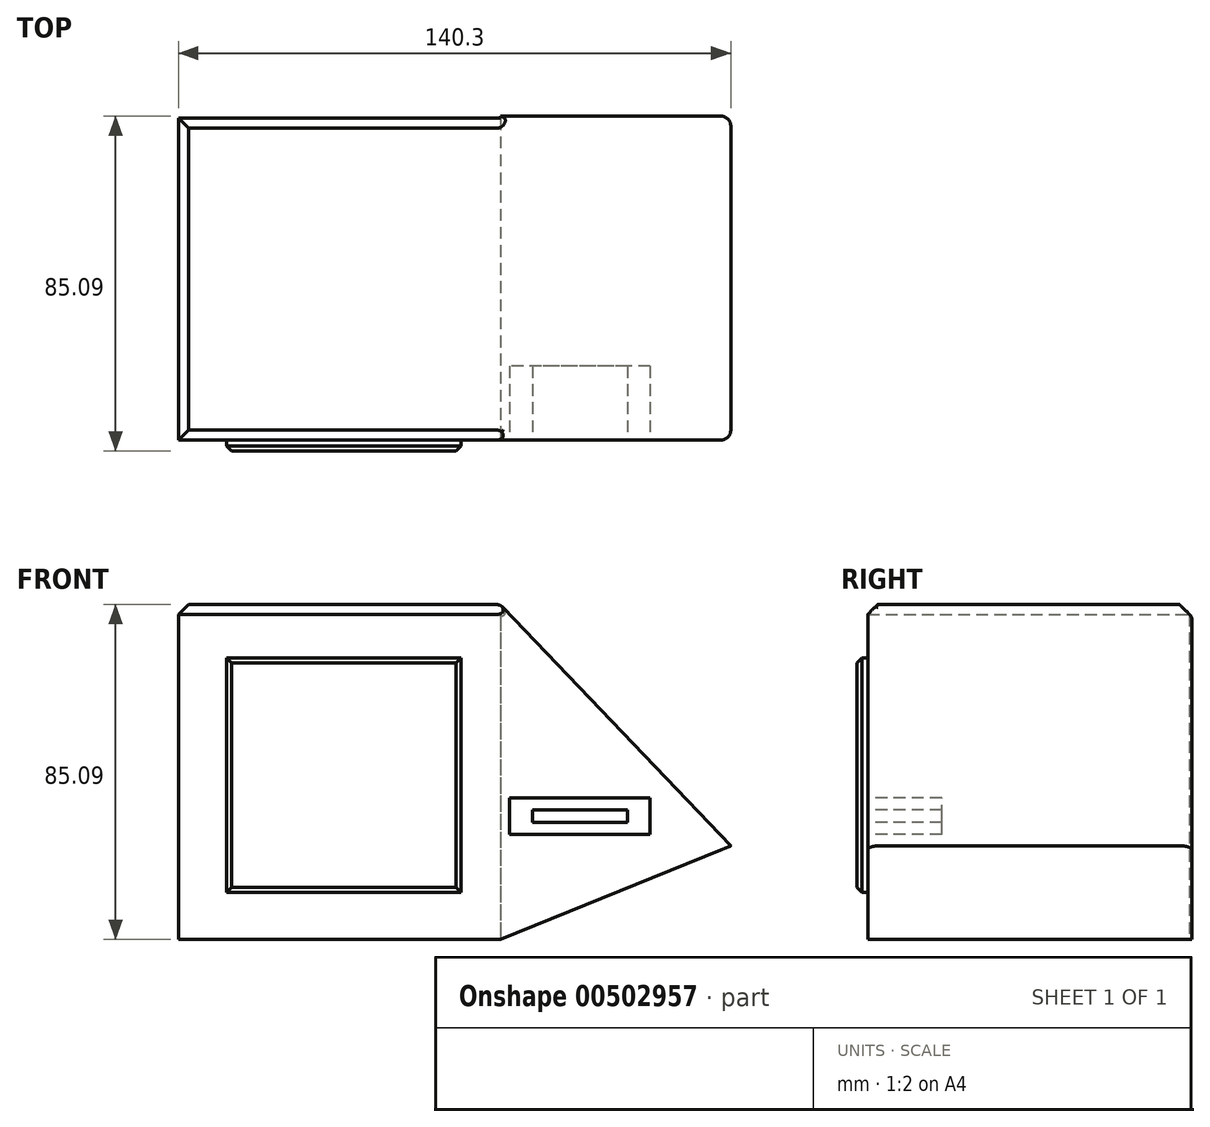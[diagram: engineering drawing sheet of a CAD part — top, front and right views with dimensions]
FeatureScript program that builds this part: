
annotation { "Feature Type Name" : "Feature", "Feature Type Description" : "" }
export const myFeature = defineFeature(function(context is Context, id is Id, definition is map)
    precondition{}
    {
        {
            var Q0;
            Q0=qCreatedBy(makeId("Top.planeOp"),FACE);
            var sketch = newSketch(context, id + "F0", { "sketchPlane" : qUnion([Q0])});
            skCircle(sketch, "E0.cCircle", {"center": v(0, 0) * mm, "radius": 40.87 * mm, "construction": true});
            skLineSegment(sketch, "E0.0", {"start": v(40.87, -40.87) * mm, "end": v(-40.87, -40.87) * mm});
            skLineSegment(sketch, "E0.1", {"start": v(-40.87, -40.87) * mm, "end": v(-40.87, 40.87) * mm});
            skLineSegment(sketch, "E0.2", {"start": v(-40.87, 40.87) * mm, "end": v(40.87, 40.87) * mm});
            skLineSegment(sketch, "E0.3", {"start": v(40.87, 40.87) * mm, "end": v(40.87, -40.87) * mm});
            skPoint(sketch, "E0.0.midPoint", {"position": v(0, -40.87) * mm});
            skSolve(sketch);
        }
        {
            var Q0;
            Q0=makeQuery(id+"F0.imprint","IMPRINT",FACE,{"disambiguationData":[TD([[makeQuery(id+"F0.imprint","IMPRINT",EDGE,{"derivedFrom":sQuery(id+"F0.wireOp",EDGE,"E0.0")}),-1.0]])]});
            extrude(context, id + "F1", {"entities" : qUnion([Q0]), "depth" : 85.1 * mm});
        }
        {
            var Q0;
            Q0=makeQuery(id+"F1.opExtrude","SWEPT_FACE",FACE,{"disambiguationData":[OSD([sQuery(id+"F0.wireOp",EDGE,"E0.0")])]});
            var sketch = newSketch(context, id + "F2", { "sketchPlane" : qUnion([Q0])});
            skLineSegment(sketch, "E1", {"start": v(40.87, 0) * mm, "end": v(99.43, 23.75) * mm});
            skLineSegment(sketch, "E2", {"start": v(99.43, 23.75) * mm, "end": v(40.87, 85.1) * mm});
            skSolve(sketch);
        }
        {
            var Q0;
            Q0 = qSketchRegion(id + "F2", true);
            var Q1;
            Q1=makeQuery(id+"F2.imprint","IMPRINT",FACE,{"disambiguationData":[TD([[makeQuery(id+"F2.imprint","IMPRINT",EDGE,{"derivedFrom":sQuery(id+"F2.wireOp",EDGE,"E1")}),1.0]])]});
            extrude(context, id + "F3", {"entities" : qUnion([Q0, Q1]), "operationType" : NewBodyOperationType.ADD, "oppositeDirection" : true, "depth" : 82.3 * mm});
        }
        {
            var Q0;
            {var subQ0=sQuery(id+"F0.wireOp",EDGE,"E0.0");Q0=makeQuery(id+"F3.boolean.opBoolean","MERGE",FACE,{"derivedFrom":[makeQuery(id+"F1.opExtrude","SWEPT_FACE",FACE,{"disambiguationData":[OSD([subQ0])]}),makeQuery(id+"F3.opExtrude","CAP_FACE",FACE,{"disambiguationData":[OSD([subQ0,sQuery(id+"F0.wireOp",EDGE,"E0.3"),sQuery(id+"F2.wireOp",EDGE,"E1"),sQuery(id+"F2.wireOp",EDGE,"E2")])],"isStart":true})]});}
            var sketch = newSketch(context, id + "F4", { "sketchPlane" : qUnion([Q0])});
            skLineSegment(sketch, "E3", {"start": v(40.87, 85.1) * mm, "end": v(40.87, 0) * mm});
            skSolve(sketch);
        }
        {
            var Q0;
            Q0=makeQuery(id+"F4.imprint","IMPRINT",FACE,{"disambiguationData":[TD([[makeQuery(id+"F4.imprint","IMPRINT",EDGE,{"derivedFrom":sQuery(id+"F4.wireOp",EDGE,"E3")}),-1.0]])]});
            var sketch = newSketch(context, id + "F5", { "sketchPlane" : qUnion([Q0])});
            skCircle(sketch, "E4.cCircle", {"center": v(1.1, 41.74) * mm, "radius": 29.8 * mm, "construction": true});
            skLineSegment(sketch, "E4.0", {"start": v(30.9, 11.95) * mm, "end": v(-28.7, 11.95) * mm});
            skLineSegment(sketch, "E4.1", {"start": v(-28.7, 11.95) * mm, "end": v(-28.7, 71.53) * mm});
            skLineSegment(sketch, "E4.2", {"start": v(-28.7, 71.53) * mm, "end": v(30.9, 71.53) * mm});
            skLineSegment(sketch, "E4.3", {"start": v(30.9, 71.53) * mm, "end": v(30.9, 11.95) * mm});
            skPoint(sketch, "E4.0.midPoint", {"position": v(1.1, 11.95) * mm});
            skLineSegment(sketch, "E5.bottom", {"start": v(81.5, 22.08) * mm, "end": v(45.06, 22.08) * mm});
            skLineSegment(sketch, "E5.top", {"start": v(81.5, 28.44) * mm, "end": v(45.06, 28.44) * mm});
            skLineSegment(sketch, "E5.left", {"start": v(81.5, 22.08) * mm, "end": v(81.5, 28.44) * mm});
            skLineSegment(sketch, "E5.right", {"start": v(45.06, 22.08) * mm, "end": v(45.06, 28.44) * mm});
            skPoint(sketch, "E5.middle", {"position": v(63.28, 25.26) * mm});
            skLineSegment(sketch, "E6.bottom", {"start": v(74.85, 25.26) * mm, "end": v(51.72, 25.26) * mm});
            skLineSegment(sketch, "E6.top", {"start": v(74.85, 25.26) * mm, "end": v(51.72, 25.26) * mm});
            skLineSegment(sketch, "E6.left", {"start": v(74.85, 25.26) * mm, "end": v(74.85, 25.26) * mm});
            skLineSegment(sketch, "E6.right", {"start": v(51.72, 25.26) * mm, "end": v(51.72, 25.26) * mm});
            skLineSegment(sketch, "E7.bottom", {"start": v(58.66, 33.93) * mm, "end": v(44.2, 33.93) * mm});
            skLineSegment(sketch, "E7.top", {"start": v(58.66, 44.92) * mm, "end": v(44.2, 44.92) * mm});
            skLineSegment(sketch, "E7.left", {"start": v(58.66, 33.93) * mm, "end": v(58.66, 44.92) * mm});
            skLineSegment(sketch, "E7.right", {"start": v(44.2, 33.93) * mm, "end": v(44.2, 44.92) * mm});
            skPoint(sketch, "E7.middle", {"position": v(51.43, 39.43) * mm});
            skCircle(sketch, "E8", {"center": v(68.5, 38.56) * mm, "radius": 4.02 * mm});
            skCircle(sketch, "E9", {"center": v(49.98, 55.91) * mm, "radius": 6.4 * mm});
            skSolve(sketch);
        }
        {
            var Q0;
            Q0=makeQuery(id+"F1.opExtrude","CAP_EDGE",EDGE,{"disambiguationData":[OSD([sQuery(id+"F0.wireOp",EDGE,"E0.0")])],"isStart":false});
            var Q1;
            Q1=makeQuery(id+"F1.opExtrude","CAP_EDGE",EDGE,{"disambiguationData":[OSD([sQuery(id+"F0.wireOp",EDGE,"E0.1")])],"isStart":false});
            var Q2;
            Q2=makeQuery(id+"F1.opExtrude","CAP_EDGE",EDGE,{"disambiguationData":[OSD([sQuery(id+"F0.wireOp",EDGE,"E0.2")])],"isStart":false});
            chamfer(context, id + "F6", {"entities" : qUnion([Q0, Q1, Q2]), "width" : 2.54 * mm, "tangentPropagation" : true});
        }
        {
            var Q0;
            {var subQ0=sQuery(id+"F0.wireOp",EDGE,"E0.3");Q0=makeQuery(id+"F3.boolean.opBoolean","MERGE",EDGE,{"derivedFrom":[makeQuery(id+"F1.opExtrude","CAP_EDGE",EDGE,{"disambiguationData":[OSD([subQ0])],"isStart":false}),makeQuery(id+"F3.opExtrude","SWEPT_EDGE",EDGE,{"disambiguationData":[OSD([sQuery(id+"F0.wireOp",EDGE,"E0.0"),subQ0,sQuery(id+"F2.wireOp",EDGE,"E2")])]})]});}
            var Q1;
            Q1=makeQuery(id+"F3.opExtrude","CAP_EDGE",EDGE,{"disambiguationData":[OSD([sQuery(id+"F2.wireOp",EDGE,"E2")])],"isStart":true});
            var Q2;
            Q2=makeQuery(id+"F3.opExtrude","CAP_EDGE",EDGE,{"disambiguationData":[OSD([sQuery(id+"F2.wireOp",EDGE,"E2")])],"isStart":false});
            fillet(context, id + "F7", {"entities" : qUnion([Q0, Q1, Q2]), "radius" : 2.54 * mm, "tangentPropagation" : true, "allowEdgeOverflow" : false});
        }
        {
            var Q0;
            Q0=makeQuery(id+"F5.imprint","IMPRINT",FACE,{"disambiguationData":[TD([[makeQuery(id+"F5.imprint","IMPRINT",EDGE,{"derivedFrom":sQuery(id+"F5.wireOp",EDGE,"E4.0")}),-1.0]])]});
            extrude(context, id + "F8", {"entities" : qUnion([Q0]), "operationType" : NewBodyOperationType.ADD, "depth" : 2.8 * mm});
        }
        {
            var Q0;
            Q0=makeQuery(id+"F8.opExtrude","CAP_EDGE",EDGE,{"disambiguationData":[OSD([sQuery(id+"F5.wireOp",EDGE,"E4.2")])],"isStart":false});
            var Q1;
            Q1=makeQuery(id+"F8.opExtrude","CAP_EDGE",EDGE,{"disambiguationData":[OSD([sQuery(id+"F5.wireOp",EDGE,"E4.3")])],"isStart":false});
            var Q2;
            Q2=makeQuery(id+"F8.opExtrude","CAP_EDGE",EDGE,{"disambiguationData":[OSD([sQuery(id+"F5.wireOp",EDGE,"E4.1")])],"isStart":false});
            var Q3;
            Q3=makeQuery(id+"F8.opExtrude","CAP_EDGE",EDGE,{"disambiguationData":[OSD([sQuery(id+"F5.wireOp",EDGE,"E4.0")])],"isStart":false});
            chamfer(context, id + "F9", {"entities" : qUnion([Q0, Q1, Q2, Q3]), "width" : 1.27 * mm, "tangentPropagation" : true});
        }
        {
            var Q0;
            Q0=makeQuery(id+"F4.imprint","IMPRINT",FACE,{"disambiguationData":[TD([[makeQuery(id+"F4.imprint","IMPRINT",EDGE,{"derivedFrom":sQuery(id+"F4.wireOp",EDGE,"E3")}),1.0]])]});
            var sketch = newSketch(context, id + "F10", { "sketchPlane" : qUnion([Q0])});
            skLineSegment(sketch, "E10.bottom", {"start": v(79.58, 26.64) * mm, "end": v(42.94, 26.64) * mm});
            skLineSegment(sketch, "E10.top", {"start": v(79.58, 34.03) * mm, "end": v(42.94, 34.03) * mm});
            skLineSegment(sketch, "E10.left", {"start": v(79.58, 26.64) * mm, "end": v(79.58, 34.03) * mm});
            skLineSegment(sketch, "E10.right", {"start": v(42.94, 26.64) * mm, "end": v(42.94, 34.03) * mm});
            skPoint(sketch, "E10.middle", {"position": v(61.26, 30.33) * mm});
            skLineSegment(sketch, "E11.bottom", {"start": v(75.24, 28.89) * mm, "end": v(47.28, 28.89) * mm});
            skLineSegment(sketch, "E11.top", {"start": v(75.24, 31.78) * mm, "end": v(47.28, 31.78) * mm});
            skLineSegment(sketch, "E11.left", {"start": v(75.24, 28.89) * mm, "end": v(75.24, 31.78) * mm});
            skLineSegment(sketch, "E11.right", {"start": v(47.28, 28.89) * mm, "end": v(47.28, 31.78) * mm});
            skSolve(sketch);
        }
        {
            var Q0;
            Q0 = qSketchRegion(id + "F10", true);
            extrude(context, id + "F11", {"entities" : qUnion([Q0]), "operationType" : NewBodyOperationType.ADD, "oppositeDirection" : true, "depth" : 17.53 * mm});
        }
        {
            var Q0;
            Q0=makeQuery(id+"F4.imprint","IMPRINT",FACE,{"disambiguationData":[TD([[makeQuery(id+"F4.imprint","IMPRINT",EDGE,{"derivedFrom":sQuery(id+"F4.wireOp",EDGE,"E3")}),1.0]])]});
            var sketch = newSketch(context, id + "F12", { "sketchPlane" : qUnion([Q0])});
            skLineSegment(sketch, "E12.bottom", {"start": v(78.94, 26.64) * mm, "end": v(43.26, 26.64) * mm});
            skLineSegment(sketch, "E12.top", {"start": v(78.94, 35.96) * mm, "end": v(43.26, 35.96) * mm});
            skLineSegment(sketch, "E12.left", {"start": v(78.94, 26.64) * mm, "end": v(78.94, 35.96) * mm});
            skLineSegment(sketch, "E12.right", {"start": v(43.26, 26.64) * mm, "end": v(43.26, 35.96) * mm});
            skPoint(sketch, "E12.middle", {"position": v(61.1, 31.3) * mm});
            skLineSegment(sketch, "E13.bottom", {"start": v(73.15, 29.69) * mm, "end": v(49.05, 29.69) * mm});
            skLineSegment(sketch, "E13.top", {"start": v(73.15, 32.9) * mm, "end": v(49.05, 32.9) * mm});
            skLineSegment(sketch, "E13.left", {"start": v(73.15, 29.69) * mm, "end": v(73.15, 32.9) * mm});
            skLineSegment(sketch, "E13.right", {"start": v(49.05, 29.69) * mm, "end": v(49.05, 32.9) * mm});
            skSolve(sketch);
        }
        {
            var Q0;
            Q0 = qSketchRegion(id + "F12", true);
            extrude(context, id + "F13", {"entities" : qUnion([Q0]), "operationType" : NewBodyOperationType.REMOVE, "oppositeDirection" : true, "depth" : 18.8 * mm});
        }
    });
